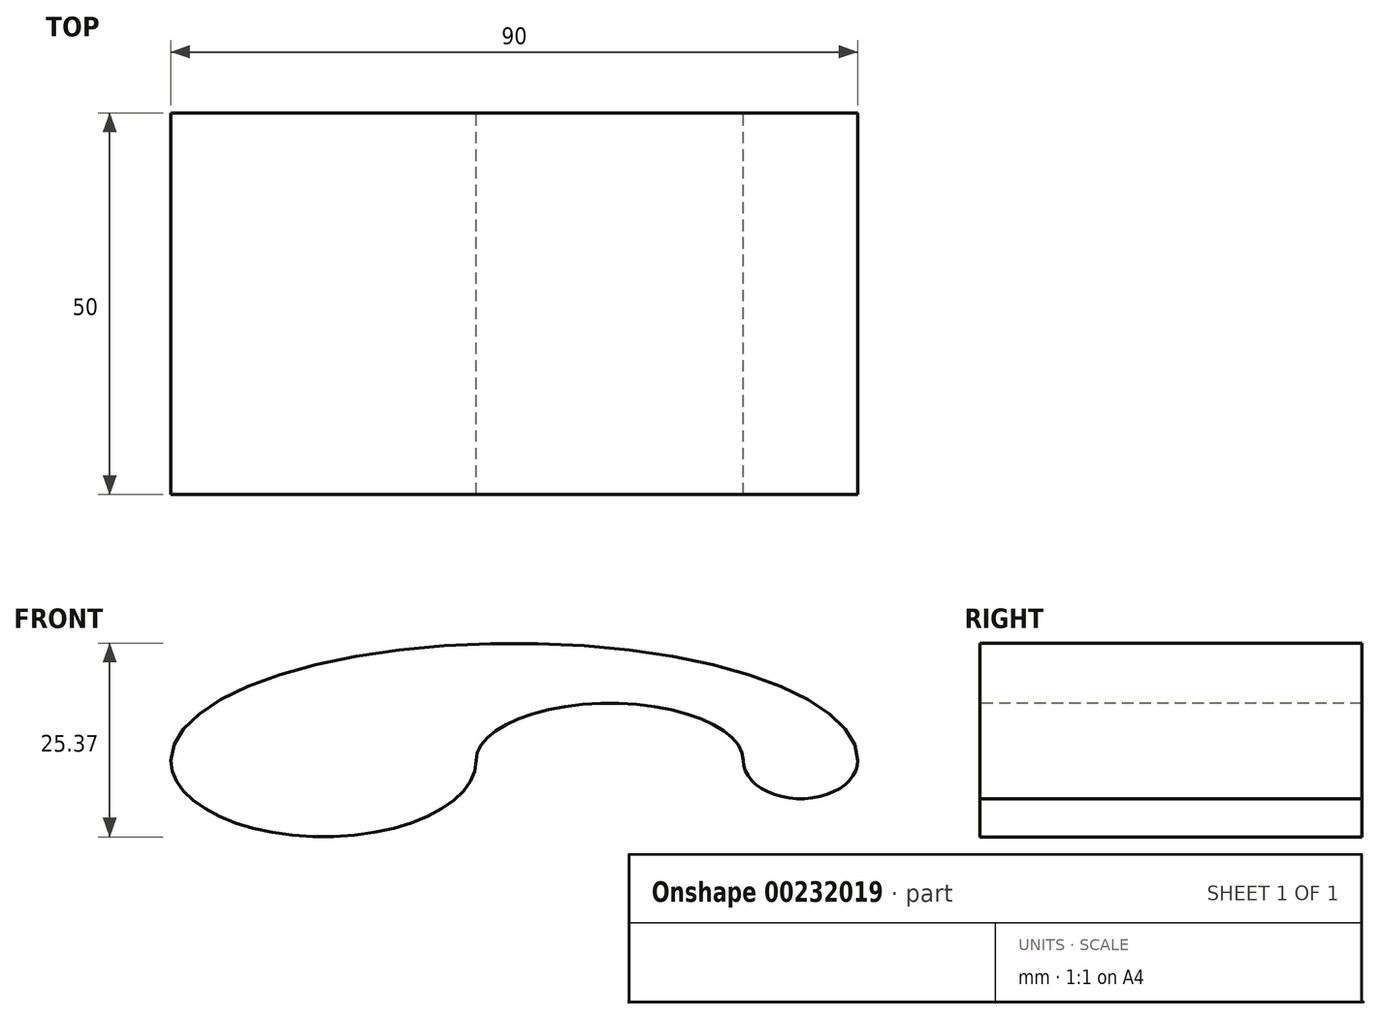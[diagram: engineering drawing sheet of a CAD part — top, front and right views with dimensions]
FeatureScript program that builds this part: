
annotation { "Feature Type Name" : "Feature", "Feature Type Description" : "" }
export const myFeature = defineFeature(function(context is Context, id is Id, definition is map)
    precondition{}
    {
        {
            var Q0;
            Q0=qCreatedBy(makeId("Front.planeOp"),FACE);
            var sketch = newSketch(context, id + "F0", { "sketchPlane" : qUnion([Q0])});
            skEllipticalArc(sketch, "E0", {});
            skEllipticalArc(sketch, "E1", {});
            skEllipticalArc(sketch, "E2", {});
            skEllipticalArc(sketch, "E3", {});
            skPoint(sketch, "E4", {"position": v(0, 0) * mm});
            const initialGuessF0  = {"E0": [-0.045, 0, 1, 0, 0.045, 0.015368052056841053, 0, 3.141592653589793], "E1": [-0.07, 0, -1, 0, 0.02, 0.01, 0, 3.141592653589793], "E2": [-0.0325, 0, -1, 0, 0.0175, 0.0075, 3.141592653589793, 0], "E3": [-0.0075, 0, -1, 0, 0.0075, 0.005, 0, 3.141592653589793]};
            skSetInitialGuess(sketch, initialGuessF0);
            skSolve(sketch);
        }
        {
            var Q0;
            Q0 = qSketchRegion(id + "F0", true);
            extrude(context, id + "F1", {"entities" : qUnion([Q0]), "depth" : 50 * mm});
        }
    });
